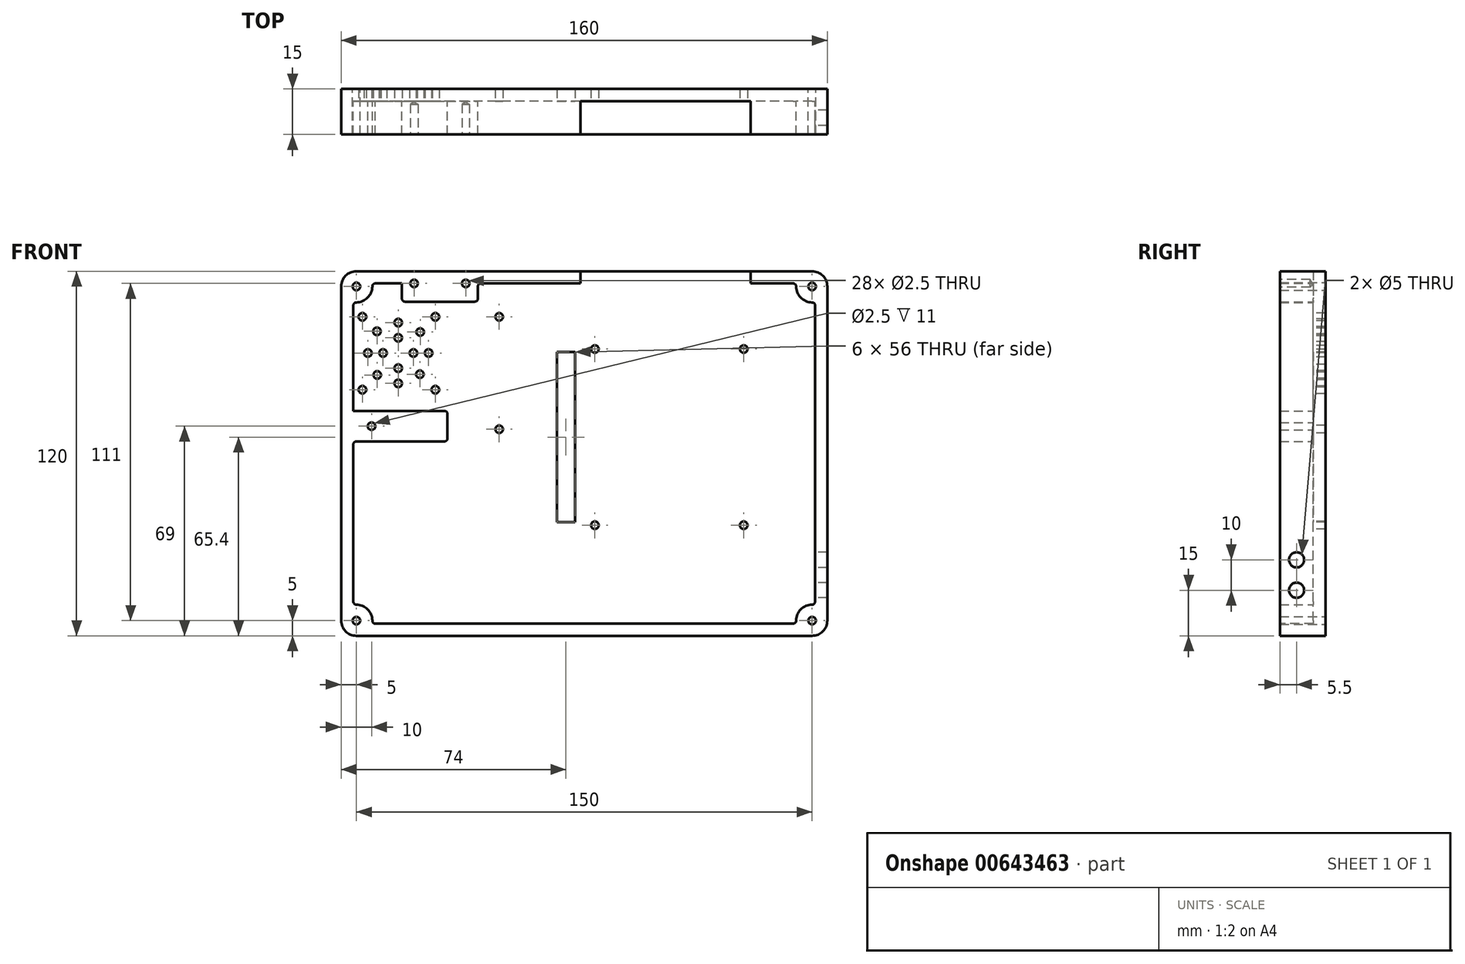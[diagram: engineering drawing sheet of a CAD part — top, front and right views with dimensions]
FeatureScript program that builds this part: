
annotation { "Feature Type Name" : "Feature", "Feature Type Description" : "" }
export const myFeature = defineFeature(function(context is Context, id is Id, definition is map)
    precondition{}
    {
        {
            var Q0;
            Q0=qCreatedBy(makeId("Front.planeOp"),FACE);
            var sketch = newSketch(context, id + "F0", { "sketchPlane" : qUnion([Q0])});
            skLineSegment(sketch, "E0.bottom", {"start": v(75, -60) * mm, "end": v(-75, -60) * mm});
            skLineSegment(sketch, "E0.top", {"start": v(75, 60) * mm, "end": v(-75, 60) * mm});
            skLineSegment(sketch, "E0.left", {"start": v(80, -55) * mm, "end": v(80, 55) * mm});
            skLineSegment(sketch, "E0.right", {"start": v(-80, -55) * mm, "end": v(-80, 55) * mm});
            skPoint(sketch, "E0.middle", {"position": v(0, 0) * mm});
            skPoint(sketch, "E1.visualSharp", {"position": v(-80, 60) * mm});
            skArc(sketch, "E1.filletArc", {"start": v(-75, 60) * mm, "mid": v(-78.54, 58.54) * mm, "end": v(-80, 55) * mm});
            skPoint(sketch, "E2.visualSharp", {"position": v(80, 60) * mm});
            skArc(sketch, "E2.filletArc", {"start": v(80, 55) * mm, "mid": v(78.54, 58.54) * mm, "end": v(75, 60) * mm});
            skPoint(sketch, "E3.visualSharp", {"position": v(80, -60) * mm});
            skArc(sketch, "E3.filletArc", {"start": v(75, -60) * mm, "mid": v(78.54, -58.54) * mm, "end": v(80, -55) * mm});
            skPoint(sketch, "E4.visualSharp", {"position": v(-80, -60) * mm});
            skArc(sketch, "E4.filletArc", {"start": v(-80, -55) * mm, "mid": v(-78.54, -58.54) * mm, "end": v(-75, -60) * mm});
            skSolve(sketch);
        }
        {
            var Q0;
            Q0=makeQuery(id+"F0.imprint","IMPRINT",FACE,{"disambiguationData":[TD([[makeQuery(id+"F0.imprint","IMPRINT",EDGE,{"derivedFrom":sQuery(id+"F0.wireOp",EDGE,"E0.bottom")}),-1.0]])]});
            extrude(context, id + "F1", {"entities" : qUnion([Q0]), "depth" : 15 * mm, "offsetDistance" : 25 * mm});
        }
        {
            var Q0;
            Q0=qCreatedBy(makeId("Front.planeOp"),FACE);
            var sketch = newSketch(context, id + "F2", { "sketchPlane" : qUnion([Q0])});
            skCircle(sketch, "E5", {"center": v(-75, 55) * mm, "radius": 1.25 * mm});
            skCircle(sketch, "E6", {"center": v(75, 55) * mm, "radius": 1.25 * mm});
            skCircle(sketch, "E7", {"center": v(75, -55) * mm, "radius": 1.25 * mm});
            skCircle(sketch, "E8", {"center": v(-75, -55) * mm, "radius": 1.25 * mm});
            skSolve(sketch);
        }
        {
            var Q0;
            Q0 = qSketchRegion(id + "F2", true);
            extrude(context, id + "F3", {"entities" : qUnion([Q0]), "operationType" : NewBodyOperationType.REMOVE, "depth" : 25 * mm, "offsetDistance" : 25 * mm});
        }
        {
            var Q0;
            Q0=makeQuery(id+"F1.opExtrude","CAP_FACE",FACE,{"disambiguationData":[OSD([sQuery(id+"F0.wireOp",EDGE,"E0.bottom"),sQuery(id+"F0.wireOp",EDGE,"E0.top"),sQuery(id+"F0.wireOp",EDGE,"E0.left"),sQuery(id+"F0.wireOp",EDGE,"E0.right"),sQuery(id+"F0.wireOp",EDGE,"E1.filletArc"),sQuery(id+"F0.wireOp",EDGE,"E2.filletArc"),sQuery(id+"F0.wireOp",EDGE,"E3.filletArc"),sQuery(id+"F0.wireOp",EDGE,"E4.filletArc")])],"isStart":false});
            shell(context, id + "F4", {"entities" : qUnion([Q0]), "thickness" : 4 * mm});
        }
        {
            var Q0;
            Q0=makeQuery(id+"F4.opShell","OFFSET_FACE",FACE,{"disambiguationData":[OSD([sQuery(id+"F0.wireOp",EDGE,"E0.bottom"),sQuery(id+"F0.wireOp",EDGE,"E0.top"),sQuery(id+"F0.wireOp",EDGE,"E0.left"),sQuery(id+"F0.wireOp",EDGE,"E0.right"),sQuery(id+"F0.wireOp",EDGE,"E1.filletArc"),sQuery(id+"F0.wireOp",EDGE,"E2.filletArc"),sQuery(id+"F0.wireOp",EDGE,"E3.filletArc"),sQuery(id+"F0.wireOp",EDGE,"E4.filletArc")])]});
            var sketch = newSketch(context, id + "F5", { "sketchPlane" : qUnion([Q0])});
            skPoint(sketch, "E9.start.orphan", {"position": v(0, -27.1) * mm});
            skCircle(sketch, "E10", {"center": v(3.5, 34.4) * mm, "radius": 1.25 * mm});
            skCircle(sketch, "E11", {"center": v(52.5, 34.4) * mm, "radius": 1.25 * mm});
            skCircle(sketch, "E12", {"center": v(52.5, -23.6) * mm, "radius": 1.25 * mm});
            skCircle(sketch, "E13", {"center": v(3.5, -23.6) * mm, "radius": 1.25 * mm});
            skSolve(sketch);
        }
        {
            var Q0;
            Q0=makeQuery(id+"F5.imprint","IMPRINT",FACE,{"disambiguationData":[TD([[makeQuery(id+"F5.imprint","IMPRINT",EDGE,{"derivedFrom":sQuery(id+"F5.wireOp",EDGE,"E10")}),1.0]])]});
            var Q1;
            Q1=makeQuery(id+"F5.imprint","IMPRINT",FACE,{"disambiguationData":[TD([[makeQuery(id+"F5.imprint","IMPRINT",EDGE,{"derivedFrom":sQuery(id+"F5.wireOp",EDGE,"E11")}),1.0]])]});
            var Q2;
            Q2=makeQuery(id+"F5.imprint","IMPRINT",FACE,{"disambiguationData":[TD([[makeQuery(id+"F5.imprint","IMPRINT",EDGE,{"derivedFrom":sQuery(id+"F5.wireOp",EDGE,"E12")}),1.0]])]});
            var Q3;
            Q3=makeQuery(id+"F5.imprint","IMPRINT",FACE,{"disambiguationData":[TD([[makeQuery(id+"F5.imprint","IMPRINT",EDGE,{"derivedFrom":sQuery(id+"F5.wireOp",EDGE,"E13")}),1.0]])]});
            extrude(context, id + "F6", {"entities" : qUnion([Q0, Q1, Q2, Q3]), "operationType" : NewBodyOperationType.REMOVE, "oppositeDirection" : true, "depth" : 25 * mm, "offsetDistance" : 25 * mm});
        }
        {
            var Q0;
            Q0=makeQuery(id+"F4.opShell","OFFSET_FACE",FACE,{"disambiguationData":[OSD([sQuery(id+"F0.wireOp",EDGE,"E0.bottom"),sQuery(id+"F0.wireOp",EDGE,"E0.top"),sQuery(id+"F0.wireOp",EDGE,"E0.left"),sQuery(id+"F0.wireOp",EDGE,"E0.right"),sQuery(id+"F0.wireOp",EDGE,"E1.filletArc"),sQuery(id+"F0.wireOp",EDGE,"E2.filletArc"),sQuery(id+"F0.wireOp",EDGE,"E3.filletArc"),sQuery(id+"F0.wireOp",EDGE,"E4.filletArc")])]});
            var sketch = newSketch(context, id + "F7", { "sketchPlane" : qUnion([Q0])});
            skLineSegment(sketch, "E14", {"start": v(-1.25, 60) * mm, "end": v(-1.25, 56) * mm});
            skLineSegment(sketch, "E15", {"start": v(54.75, 60) * mm, "end": v(54.75, 56) * mm});
            skLineSegment(sketch, "E16.0", {"start": v(54.75, 60) * mm, "end": v(-1.25, 60) * mm});
            skLineSegment(sketch, "E17.0", {"start": v(54.75, 56) * mm, "end": v(-1.25, 56) * mm});
            skPoint(sketch, "E18.orphan", {"position": v(69.85, 56) * mm});
            skPoint(sketch, "E19.orphan", {"position": v(-69.85, 56) * mm});
            skSolve(sketch);
        }
        {
            var Q0;
            Q0=makeQuery(id+"F7.imprint","IMPRINT",FACE,{"disambiguationData":[TD([[makeQuery(id+"F7.imprint","IMPRINT",EDGE,{"derivedFrom":sQuery(id+"F7.wireOp",EDGE,"E14")}),1.0]])]});
            extrude(context, id + "F8", {"entities" : qUnion([Q0]), "operationType" : NewBodyOperationType.REMOVE, "depth" : 25 * mm, "offsetDistance" : 25 * mm});
        }
        {
            var Q0;
            Q0=makeQuery(id+"F8.boolean.opBoolean","MERGE",FACE,{"derivedFrom":[makeQuery(id+"F4.opShell","OFFSET_FACE",FACE,{"disambiguationData":[OSD([sQuery(id+"F0.wireOp",EDGE,"E0.bottom"),sQuery(id+"F0.wireOp",EDGE,"E0.top"),sQuery(id+"F0.wireOp",EDGE,"E0.left"),sQuery(id+"F0.wireOp",EDGE,"E0.right"),sQuery(id+"F0.wireOp",EDGE,"E1.filletArc"),sQuery(id+"F0.wireOp",EDGE,"E2.filletArc"),sQuery(id+"F0.wireOp",EDGE,"E3.filletArc"),sQuery(id+"F0.wireOp",EDGE,"E4.filletArc")])]}),makeQuery(id+"F8.opExtrude","CAP_FACE",FACE,{"disambiguationData":[OSD([sQuery(id+"F7.wireOp",EDGE,"E14"),sQuery(id+"F7.wireOp",EDGE,"E15"),sQuery(id+"F7.wireOp",EDGE,"E16.0"),sQuery(id+"F7.wireOp",EDGE,"E17.0")])],"isStart":true})]});
            var sketch = newSketch(context, id + "F9", { "sketchPlane" : qUnion([Q0])});
            skLineSegment(sketch, "E20.0", {"start": v(-35, 56) * mm, "end": v(-60, 56) * mm});
            skLineSegment(sketch, "E21", {"start": v(-60, 56) * mm, "end": v(-60, 50) * mm});
            skLineSegment(sketch, "E22", {"start": v(-35, 56) * mm, "end": v(-35, 50) * mm});
            skLineSegment(sketch, "E23", {"start": v(-60, 50) * mm, "end": v(-35, 50) * mm});
            skPoint(sketch, "E24.orphan", {"position": v(-69.85, 56) * mm});
            skPoint(sketch, "E25.orphan", {"position": v(-1.25, 56) * mm});
            skSolve(sketch);
        }
        {
            var Q0;
            Q0 = qSketchRegion(id + "F9", true);
            extrude(context, id + "F10", {"entities" : qUnion([Q0]), "operationType" : NewBodyOperationType.ADD, "depth" : 11 * mm, "offsetDistance" : 25 * mm});
        }
        {
            var Q0;
            Q0=makeQuery(id+"F10.opExtrude","SWEPT_EDGE",EDGE,{"disambiguationData":[OSD([sQuery(id+"F0.wireOp",EDGE,"E0.top"),sQuery(id+"F9.wireOp",EDGE,"E20.0"),sQuery(id+"F9.wireOp",EDGE,"E21")])]});
            var Q1;
            Q1=makeQuery(id+"F10.opExtrude","SWEPT_EDGE",EDGE,{"disambiguationData":[OSD([sQuery(id+"F9.wireOp",EDGE,"E21"),sQuery(id+"F9.wireOp",EDGE,"E23")])]});
            var Q2;
            Q2=makeQuery(id+"F10.opExtrude","SWEPT_EDGE",EDGE,{"disambiguationData":[OSD([sQuery(id+"F9.wireOp",EDGE,"E22"),sQuery(id+"F9.wireOp",EDGE,"E23")])]});
            var Q3;
            Q3=makeQuery(id+"F10.opExtrude","SWEPT_EDGE",EDGE,{"disambiguationData":[OSD([sQuery(id+"F0.wireOp",EDGE,"E0.top"),sQuery(id+"F9.wireOp",EDGE,"E20.0"),sQuery(id+"F9.wireOp",EDGE,"E22")])]});
            fillet(context, id + "F11", {"entities" : qUnion([Q0, Q1, Q2, Q3]), "radius" : 1 * mm, "tangentPropagation" : true, "allowEdgeOverflow" : false});
        }
        {
            var Q0;
            Q0=makeQuery(id+"F10.boolean.opBoolean","MERGE",FACE,{"derivedFrom":[makeQuery(id+"F1.opExtrude","CAP_FACE",FACE,{"disambiguationData":[OSD([sQuery(id+"F0.wireOp",EDGE,"E0.bottom"),sQuery(id+"F0.wireOp",EDGE,"E0.top"),sQuery(id+"F0.wireOp",EDGE,"E0.left"),sQuery(id+"F0.wireOp",EDGE,"E0.right"),sQuery(id+"F0.wireOp",EDGE,"E1.filletArc"),sQuery(id+"F0.wireOp",EDGE,"E2.filletArc"),sQuery(id+"F0.wireOp",EDGE,"E3.filletArc"),sQuery(id+"F0.wireOp",EDGE,"E4.filletArc")])],"isStart":false}),makeQuery(id+"F10.opExtrude","CAP_FACE",FACE,{"disambiguationData":[OSD([sQuery(id+"F9.wireOp",EDGE,"E20.0"),sQuery(id+"F9.wireOp",EDGE,"E21"),sQuery(id+"F9.wireOp",EDGE,"E22"),sQuery(id+"F9.wireOp",EDGE,"E23")])],"isStart":false})]});
            var sketch = newSketch(context, id + "F12", { "sketchPlane" : qUnion([Q0])});
            skCircle(sketch, "E26", {"center": v(-56, 56) * mm, "radius": 1.25 * mm});
            skCircle(sketch, "E27", {"center": v(-39, 56) * mm, "radius": 1.25 * mm});
            skSolve(sketch);
        }
        {
            var Q0;
            Q0=sQuery(id+"F12.wireOp",VERTEX,"E26.center");
            var Q1;
            Q1=sQuery(id+"F12.wireOp",VERTEX,"E27.center");
            var Q2;
            Q2=makeQuery(id+"F1.opExtrude","SWEPT_BODY",BODY,{"disambiguationData":[OSD([sQuery(id+"F0.wireOp",EDGE,"E0.bottom"),sQuery(id+"F0.wireOp",EDGE,"E0.top"),sQuery(id+"F0.wireOp",EDGE,"E0.left"),sQuery(id+"F0.wireOp",EDGE,"E0.right"),sQuery(id+"F0.wireOp",EDGE,"E1.filletArc"),sQuery(id+"F0.wireOp",EDGE,"E2.filletArc"),sQuery(id+"F0.wireOp",EDGE,"E3.filletArc"),sQuery(id+"F0.wireOp",EDGE,"E4.filletArc")])]});
            hole(context, id + "F13", {"style" : HoleStyle.SIMPLE, "endStyle" : HoleEndStyle.BLIND, "holeDiameter" : 2.5 * mm, "majorDiameter" : 5 * mm, "holeDepth" : 10 * mm, "isTappedThrough" : true, "tappedDepth" : 12 * mm, "tapClearance" : 3, "startFromSketch" : true, "locations" : qUnion([Q0, Q1]), "scope" : qUnion([Q2])});
        }
        {
            var Q0;
            Q0=makeQuery(id+"F8.boolean.opBoolean","MERGE",FACE,{"derivedFrom":[makeQuery(id+"F4.opShell","OFFSET_FACE",FACE,{"disambiguationData":[OSD([sQuery(id+"F0.wireOp",EDGE,"E0.bottom"),sQuery(id+"F0.wireOp",EDGE,"E0.top"),sQuery(id+"F0.wireOp",EDGE,"E0.left"),sQuery(id+"F0.wireOp",EDGE,"E0.right"),sQuery(id+"F0.wireOp",EDGE,"E1.filletArc"),sQuery(id+"F0.wireOp",EDGE,"E2.filletArc"),sQuery(id+"F0.wireOp",EDGE,"E3.filletArc"),sQuery(id+"F0.wireOp",EDGE,"E4.filletArc")])]}),makeQuery(id+"F8.opExtrude","CAP_FACE",FACE,{"disambiguationData":[OSD([sQuery(id+"F7.wireOp",EDGE,"E14"),sQuery(id+"F7.wireOp",EDGE,"E15"),sQuery(id+"F7.wireOp",EDGE,"E16.0"),sQuery(id+"F7.wireOp",EDGE,"E17.0")])],"isStart":true})]});
            var sketch = newSketch(context, id + "F14", { "sketchPlane" : qUnion([Q0])});
            skCircle(sketch, "E28", {"center": v(-73, 45) * mm, "radius": 1.25 * mm});
            skCircle(sketch, "E29", {"center": v(-49, 45) * mm, "radius": 1.25 * mm});
            skCircle(sketch, "E30", {"center": v(-49, 21) * mm, "radius": 1.25 * mm});
            skCircle(sketch, "E31", {"center": v(-73, 21) * mm, "radius": 1.25 * mm});
            skSolve(sketch);
        }
        {
            var Q0;
            Q0=sQuery(id+"F14.wireOp",VERTEX,"E29.center");
            var Q1;
            Q1=sQuery(id+"F14.wireOp",VERTEX,"E28.center");
            var Q2;
            Q2=sQuery(id+"F14.wireOp",VERTEX,"E31.center");
            var Q3;
            Q3=sQuery(id+"F14.wireOp",VERTEX,"E30.center");
            var Q4;
            Q4=makeQuery(id+"F1.opExtrude","SWEPT_BODY",BODY,{"disambiguationData":[OSD([sQuery(id+"F0.wireOp",EDGE,"E0.bottom"),sQuery(id+"F0.wireOp",EDGE,"E0.top"),sQuery(id+"F0.wireOp",EDGE,"E0.left"),sQuery(id+"F0.wireOp",EDGE,"E0.right"),sQuery(id+"F0.wireOp",EDGE,"E1.filletArc"),sQuery(id+"F0.wireOp",EDGE,"E2.filletArc"),sQuery(id+"F0.wireOp",EDGE,"E3.filletArc"),sQuery(id+"F0.wireOp",EDGE,"E4.filletArc")])]});
            hole(context, id + "F15", {"style" : HoleStyle.SIMPLE, "endStyle" : HoleEndStyle.BLIND, "holeDiameter" : 2.5 * mm, "majorDiameter" : 5 * mm, "holeDepth" : 10 * mm, "isTappedThrough" : true, "tappedDepth" : 12 * mm, "tapClearance" : 3, "startFromSketch" : true, "locations" : qUnion([Q0, Q1, Q2, Q3]), "scope" : qUnion([Q4])});
        }
        {
            var Q0;
            Q0=makeQuery(id+"F8.boolean.opBoolean","MERGE",FACE,{"derivedFrom":[makeQuery(id+"F4.opShell","OFFSET_FACE",FACE,{"disambiguationData":[OSD([sQuery(id+"F0.wireOp",EDGE,"E0.bottom"),sQuery(id+"F0.wireOp",EDGE,"E0.top"),sQuery(id+"F0.wireOp",EDGE,"E0.left"),sQuery(id+"F0.wireOp",EDGE,"E0.right"),sQuery(id+"F0.wireOp",EDGE,"E1.filletArc"),sQuery(id+"F0.wireOp",EDGE,"E2.filletArc"),sQuery(id+"F0.wireOp",EDGE,"E3.filletArc"),sQuery(id+"F0.wireOp",EDGE,"E4.filletArc")])]}),makeQuery(id+"F8.opExtrude","CAP_FACE",FACE,{"disambiguationData":[OSD([sQuery(id+"F7.wireOp",EDGE,"E14"),sQuery(id+"F7.wireOp",EDGE,"E15"),sQuery(id+"F7.wireOp",EDGE,"E16.0"),sQuery(id+"F7.wireOp",EDGE,"E17.0")])],"isStart":true})]});
            var sketch = newSketch(context, id + "F16", { "sketchPlane" : qUnion([Q0])});
            skLineSegment(sketch, "E32", {"start": v(-76, 4) * mm, "end": v(-46, 4) * mm});
            skLineSegment(sketch, "E33", {"start": v(-76, 14) * mm, "end": v(-46, 14) * mm});
            skLineSegment(sketch, "E34.0", {"start": v(-76, 4) * mm, "end": v(-76, 14) * mm});
            skLineSegment(sketch, "E35", {"start": v(-45, 13) * mm, "end": v(-45, 5) * mm});
            skCircle(sketch, "E36", {"center": v(-70, 9) * mm, "radius": 1.25 * mm});
            skPoint(sketch, "E37.orphan", {"position": v(-76, 49.85) * mm});
            skPoint(sketch, "E38.orphan", {"position": v(-76, -49.85) * mm});
            skPoint(sketch, "E39.visualSharp", {"position": v(-45, 14) * mm});
            skArc(sketch, "E39.filletArc", {"start": v(-45, 13) * mm, "mid": v(-45.3, 13.7) * mm, "end": v(-46, 14) * mm});
            skPoint(sketch, "E40.visualSharp", {"position": v(-45, 4) * mm});
            skArc(sketch, "E40.filletArc", {"start": v(-46, 4) * mm, "mid": v(-45.3, 4.3) * mm, "end": v(-45, 5) * mm});
            skSolve(sketch);
        }
        {
            var Q0;
            Q0 = qSketchRegion(id + "F16", true);
            extrude(context, id + "F17", {"entities" : qUnion([Q0]), "operationType" : NewBodyOperationType.ADD, "depth" : 11 * mm, "offsetDistance" : 25 * mm});
        }
        {
            var Q0;
            Q0=makeQuery(id+"F4.opShell","TWEAK_EDGE",EDGE,{"derivedFrom":[makeQuery(id+"F1.opExtrude","SWEPT_FACE",FACE,{"disambiguationData":[OSD([sQuery(id+"F0.wireOp",EDGE,"E0.top")])]}),makeQuery(id+"F3.boolean.opBoolean","COPY",FACE,{"derivedFrom":makeQuery(id+"F3.opExtrude","SWEPT_FACE",FACE,{"disambiguationData":[OSD([sQuery(id+"F2.wireOp",EDGE,"E5")])]})})]});
            var Q1;
            Q1=makeQuery(id+"F4.opShell","TWEAK_EDGE",EDGE,{"derivedFrom":[makeQuery(id+"F1.opExtrude","SWEPT_FACE",FACE,{"disambiguationData":[OSD([sQuery(id+"F0.wireOp",EDGE,"E0.right")])]}),makeQuery(id+"F3.boolean.opBoolean","COPY",FACE,{"derivedFrom":makeQuery(id+"F3.opExtrude","SWEPT_FACE",FACE,{"disambiguationData":[OSD([sQuery(id+"F2.wireOp",EDGE,"E5")])]})})]});
            var Q2;
            Q2=makeQuery(id+"F4.opShell","TWEAK_EDGE",EDGE,{"derivedFrom":[makeQuery(id+"F1.opExtrude","SWEPT_FACE",FACE,{"disambiguationData":[OSD([sQuery(id+"F0.wireOp",EDGE,"E0.right")])]}),makeQuery(id+"F3.boolean.opBoolean","COPY",FACE,{"derivedFrom":makeQuery(id+"F3.opExtrude","SWEPT_FACE",FACE,{"disambiguationData":[OSD([sQuery(id+"F2.wireOp",EDGE,"E8")])]})})]});
            var Q3;
            Q3=makeQuery(id+"F4.opShell","TWEAK_EDGE",EDGE,{"derivedFrom":[makeQuery(id+"F1.opExtrude","SWEPT_FACE",FACE,{"disambiguationData":[OSD([sQuery(id+"F0.wireOp",EDGE,"E0.bottom")])]}),makeQuery(id+"F3.boolean.opBoolean","COPY",FACE,{"derivedFrom":makeQuery(id+"F3.opExtrude","SWEPT_FACE",FACE,{"disambiguationData":[OSD([sQuery(id+"F2.wireOp",EDGE,"E8")])]})})]});
            var Q4;
            Q4=makeQuery(id+"F4.opShell","TWEAK_EDGE",EDGE,{"derivedFrom":[makeQuery(id+"F1.opExtrude","SWEPT_FACE",FACE,{"disambiguationData":[OSD([sQuery(id+"F0.wireOp",EDGE,"E0.bottom")])]}),makeQuery(id+"F3.boolean.opBoolean","COPY",FACE,{"derivedFrom":makeQuery(id+"F3.opExtrude","SWEPT_FACE",FACE,{"disambiguationData":[OSD([sQuery(id+"F2.wireOp",EDGE,"E7")])]})})]});
            var Q5;
            Q5=makeQuery(id+"F4.opShell","TWEAK_EDGE",EDGE,{"derivedFrom":[makeQuery(id+"F1.opExtrude","SWEPT_FACE",FACE,{"disambiguationData":[OSD([sQuery(id+"F0.wireOp",EDGE,"E0.left")])]}),makeQuery(id+"F3.boolean.opBoolean","COPY",FACE,{"derivedFrom":makeQuery(id+"F3.opExtrude","SWEPT_FACE",FACE,{"disambiguationData":[OSD([sQuery(id+"F2.wireOp",EDGE,"E7")])]})})]});
            var Q6;
            Q6=makeQuery(id+"F4.opShell","TWEAK_EDGE",EDGE,{"derivedFrom":[makeQuery(id+"F1.opExtrude","SWEPT_FACE",FACE,{"disambiguationData":[OSD([sQuery(id+"F0.wireOp",EDGE,"E0.left")])]}),makeQuery(id+"F3.boolean.opBoolean","COPY",FACE,{"derivedFrom":makeQuery(id+"F3.opExtrude","SWEPT_FACE",FACE,{"disambiguationData":[OSD([sQuery(id+"F2.wireOp",EDGE,"E6")])]})})]});
            var Q7;
            Q7=makeQuery(id+"F4.opShell","TWEAK_EDGE",EDGE,{"derivedFrom":[makeQuery(id+"F1.opExtrude","SWEPT_FACE",FACE,{"disambiguationData":[OSD([sQuery(id+"F0.wireOp",EDGE,"E0.top")])]}),makeQuery(id+"F3.boolean.opBoolean","COPY",FACE,{"derivedFrom":makeQuery(id+"F3.opExtrude","SWEPT_FACE",FACE,{"disambiguationData":[OSD([sQuery(id+"F2.wireOp",EDGE,"E6")])]})})]});
            var Q8;
            Q8=makeQuery(id+"F17.opExtrude","SWEPT_EDGE",EDGE,{"disambiguationData":[OSD([sQuery(id+"F0.wireOp",EDGE,"E0.right"),sQuery(id+"F16.wireOp",EDGE,"E33"),sQuery(id+"F16.wireOp",EDGE,"E34.0")])]});
            var Q9;
            Q9=makeQuery(id+"F17.opExtrude","SWEPT_EDGE",EDGE,{"disambiguationData":[OSD([sQuery(id+"F16.wireOp",EDGE,"E33"),sQuery(id+"F16.wireOp",EDGE,"E35")])]});
            var Q10;
            Q10=makeQuery(id+"F17.opExtrude","SWEPT_EDGE",EDGE,{"disambiguationData":[OSD([sQuery(id+"F16.wireOp",EDGE,"E32"),sQuery(id+"F16.wireOp",EDGE,"E35")])]});
            var Q11;
            Q11=makeQuery(id+"F17.opExtrude","SWEPT_EDGE",EDGE,{"disambiguationData":[OSD([sQuery(id+"F0.wireOp",EDGE,"E0.right"),sQuery(id+"F16.wireOp",EDGE,"E32"),sQuery(id+"F16.wireOp",EDGE,"E34.0")])]});
            fillet(context, id + "F18", {"entities" : qUnion([Q0, Q1, Q2, Q3, Q4, Q5, Q6, Q7, Q8, Q9, Q10, Q11]), "radius" : 1 * mm, "tangentPropagation" : true, "allowEdgeOverflow" : false});
        }
        {
            var Q0;
            Q0=makeQuery(id+"F8.boolean.opBoolean","MERGE",FACE,{"derivedFrom":[makeQuery(id+"F4.opShell","OFFSET_FACE",FACE,{"disambiguationData":[OSD([sQuery(id+"F0.wireOp",EDGE,"E0.bottom"),sQuery(id+"F0.wireOp",EDGE,"E0.top"),sQuery(id+"F0.wireOp",EDGE,"E0.left"),sQuery(id+"F0.wireOp",EDGE,"E0.right"),sQuery(id+"F0.wireOp",EDGE,"E1.filletArc"),sQuery(id+"F0.wireOp",EDGE,"E2.filletArc"),sQuery(id+"F0.wireOp",EDGE,"E3.filletArc"),sQuery(id+"F0.wireOp",EDGE,"E4.filletArc")])]}),makeQuery(id+"F8.opExtrude","CAP_FACE",FACE,{"disambiguationData":[OSD([sQuery(id+"F7.wireOp",EDGE,"E14"),sQuery(id+"F7.wireOp",EDGE,"E15"),sQuery(id+"F7.wireOp",EDGE,"E16.0"),sQuery(id+"F7.wireOp",EDGE,"E17.0")])],"isStart":true})]});
            var sketch = newSketch(context, id + "F19", { "sketchPlane" : qUnion([Q0])});
            skCircle(sketch, "E41", {"center": v(-61.22, 43.1) * mm, "radius": 1.5 * mm});
            skCircle(sketch, "E42.MirrorC", {"center": v(-61.22, 23.1) * mm, "radius": 1.5 * mm});
            skCircle(sketch, "E43", {"center": v(-51.22, 33.1) * mm, "radius": 1.5 * mm});
            skCircle(sketch, "E44.MirrorC", {"center": v(-71.22, 33.1) * mm, "radius": 1.5 * mm});
            skCircle(sketch, "E45", {"center": v(-61.22, 38.1) * mm, "radius": 1.5 * mm});
            skCircle(sketch, "E46", {"center": v(-56.22, 33.1) * mm, "radius": 1.5 * mm});
            skCircle(sketch, "E47.MirrorC", {"center": v(-66.22, 33.1) * mm, "radius": 1.5 * mm});
            skCircle(sketch, "E48.MirrorC", {"center": v(-61.22, 28.1) * mm, "radius": 1.5 * mm});
            skPoint(sketch, "E49.orphan", {"position": v(-73, 45) * mm});
            skPoint(sketch, "E50.orphan", {"position": v(-49, 45) * mm});
            skPoint(sketch, "E51.orphan", {"position": v(-49, 21) * mm});
            skPoint(sketch, "E52.orphan", {"position": v(-73, 21) * mm});
            skCircle(sketch, "E53", {"center": v(-68.23, 40.23) * mm, "radius": 1.5 * mm});
            skCircle(sketch, "E54", {"center": v(-54, 40) * mm, "radius": 1.5 * mm});
            skCircle(sketch, "E55", {"center": v(-54.09, 26.09) * mm, "radius": 1.5 * mm});
            skCircle(sketch, "E56", {"center": v(-68.13, 25.87) * mm, "radius": 1.5 * mm});
            skSolve(sketch);
        }
        {
            var Q0;
            Q0=sQuery(id+"F19.wireOp",VERTEX,"E41.center");
            var Q1;
            Q1=sQuery(id+"F19.wireOp",VERTEX,"E45.center");
            var Q2;
            Q2=sQuery(id+"F19.wireOp",VERTEX,"E53.center");
            var Q3;
            Q3=sQuery(id+"F19.wireOp",VERTEX,"E44.MirrorC.center");
            var Q4;
            Q4=sQuery(id+"F19.wireOp",VERTEX,"E47.MirrorC.center");
            var Q5;
            Q5=sQuery(id+"F19.wireOp",VERTEX,"E56.center");
            var Q6;
            Q6=sQuery(id+"F19.wireOp",VERTEX,"E48.MirrorC.center");
            var Q7;
            Q7=sQuery(id+"F19.wireOp",VERTEX,"E42.MirrorC.center");
            var Q8;
            Q8=sQuery(id+"F19.wireOp",VERTEX,"E54.center");
            var Q9;
            Q9=sQuery(id+"F19.wireOp",VERTEX,"E46.center");
            var Q10;
            Q10=sQuery(id+"F19.wireOp",VERTEX,"E55.center");
            var Q11;
            Q11=sQuery(id+"F19.wireOp",VERTEX,"E43.center");
            var Q12;
            Q12=makeQuery(id+"F1.opExtrude","SWEPT_BODY",BODY,{"disambiguationData":[OSD([sQuery(id+"F0.wireOp",EDGE,"E0.bottom"),sQuery(id+"F0.wireOp",EDGE,"E0.top"),sQuery(id+"F0.wireOp",EDGE,"E0.left"),sQuery(id+"F0.wireOp",EDGE,"E0.right"),sQuery(id+"F0.wireOp",EDGE,"E1.filletArc"),sQuery(id+"F0.wireOp",EDGE,"E2.filletArc"),sQuery(id+"F0.wireOp",EDGE,"E3.filletArc"),sQuery(id+"F0.wireOp",EDGE,"E4.filletArc")])]});
            hole(context, id + "F20", {"style" : HoleStyle.SIMPLE, "endStyle" : HoleEndStyle.BLIND, "holeDiameter" : 2.5 * mm, "majorDiameter" : 5 * mm, "holeDepth" : 10 * mm, "isTappedThrough" : true, "tappedDepth" : 12 * mm, "tapClearance" : 3, "startFromSketch" : true, "locations" : qUnion([Q0, Q1, Q2, Q3, Q4, Q5, Q6, Q7, Q8, Q9, Q10, Q11]), "scope" : qUnion([Q12])});
        }
        {
            var Q0;
            Q0=makeQuery(id+"F8.boolean.opBoolean","MERGE",FACE,{"derivedFrom":[makeQuery(id+"F4.opShell","OFFSET_FACE",FACE,{"disambiguationData":[OSD([sQuery(id+"F0.wireOp",EDGE,"E0.bottom"),sQuery(id+"F0.wireOp",EDGE,"E0.top"),sQuery(id+"F0.wireOp",EDGE,"E0.left"),sQuery(id+"F0.wireOp",EDGE,"E0.right"),sQuery(id+"F0.wireOp",EDGE,"E1.filletArc"),sQuery(id+"F0.wireOp",EDGE,"E2.filletArc"),sQuery(id+"F0.wireOp",EDGE,"E3.filletArc"),sQuery(id+"F0.wireOp",EDGE,"E4.filletArc")])]}),makeQuery(id+"F8.opExtrude","CAP_FACE",FACE,{"disambiguationData":[OSD([sQuery(id+"F7.wireOp",EDGE,"E14"),sQuery(id+"F7.wireOp",EDGE,"E15"),sQuery(id+"F7.wireOp",EDGE,"E16.0"),sQuery(id+"F7.wireOp",EDGE,"E17.0")])],"isStart":true})]});
            var sketch = newSketch(context, id + "F21", { "sketchPlane" : qUnion([Q0])});
            skLineSegment(sketch, "E57", {"start": v(-3, 33.4) * mm, "end": v(-3, -22.6) * mm});
            skLineSegment(sketch, "E58", {"start": v(-9, 33.4) * mm, "end": v(-9, -22.6) * mm});
            skLineSegment(sketch, "E59", {"start": v(-9, 33.4) * mm, "end": v(-3, 33.4) * mm});
            skLineSegment(sketch, "E60.MirrorCS", {"start": v(-9, -22.6) * mm, "end": v(-3, -22.6) * mm});
            skSolve(sketch);
        }
        {
            var Q0;
            Q0=makeQuery(id+"F21.imprint","IMPRINT",FACE,{"disambiguationData":[TD([[makeQuery(id+"F21.imprint","IMPRINT",EDGE,{"derivedFrom":sQuery(id+"F21.wireOp",EDGE,"E57")}),-1.0]])]});
            extrude(context, id + "F22", {"entities" : qUnion([Q0]), "operationType" : NewBodyOperationType.REMOVE, "oppositeDirection" : true, "depth" : 25 * mm, "offsetDistance" : 25 * mm});
        }
        {
            var Q0;
            Q0=qCreatedBy(makeId("Right.planeOp"),FACE);
            var sketch = newSketch(context, id + "F23", { "sketchPlane" : qUnion([Q0])});
            skCircle(sketch, "E61", {"center": v(-9.5, -35) * mm, "radius": 2.5 * mm});
            skCircle(sketch, "E62", {"center": v(-9.5, -45) * mm, "radius": 2.5 * mm});
            skSolve(sketch);
        }
        {
            var Q0;
            Q0=sQuery(id+"F23.wireOp",VERTEX,"E61.center");
            var Q1;
            Q1=sQuery(id+"F23.wireOp",VERTEX,"E62.center");
            var Q2;
            Q2=makeQuery(id+"F1.opExtrude","SWEPT_BODY",BODY,{"disambiguationData":[OSD([sQuery(id+"F0.wireOp",EDGE,"E0.bottom"),sQuery(id+"F0.wireOp",EDGE,"E0.top"),sQuery(id+"F0.wireOp",EDGE,"E0.left"),sQuery(id+"F0.wireOp",EDGE,"E0.right"),sQuery(id+"F0.wireOp",EDGE,"E1.filletArc"),sQuery(id+"F0.wireOp",EDGE,"E2.filletArc"),sQuery(id+"F0.wireOp",EDGE,"E3.filletArc"),sQuery(id+"F0.wireOp",EDGE,"E4.filletArc")])]});
            hole(context, id + "F24", {"style" : HoleStyle.SIMPLE, "endStyle" : HoleEndStyle.BLIND, "oppositeDirection" : true, "holeDiameter" : 5 * mm, "majorDiameter" : 5 * mm, "holeDepth" : 100 * mm, "isTappedThrough" : true, "tappedDepth" : 12 * mm, "tapClearance" : 3, "startFromSketch" : true, "locations" : qUnion([Q0, Q1]), "scope" : qUnion([Q2])});
        }
        {
            var Q0;
            {var subQ3=sQuery(id+"F0.wireOp",EDGE,"E0.top");var subQ5=sQuery(id+"F0.wireOp",EDGE,"E0.left");var subQ6=sQuery(id+"F0.wireOp",EDGE,"E0.bottom");var subQ7=sQuery(id+"F7.wireOp",EDGE,"E15");var subQ8=sQuery(id+"F0.wireOp",EDGE,"E0.right");var subQ9=sQuery(id+"F7.wireOp",EDGE,"E14");Q0=makeQuery(id+"F17.boolean.opBoolean","SPLIT",FACE,{"disambiguationData":[TD([makeQuery(id+"F1.opExtrude","SWEPT_FACE",FACE,{"disambiguationData":[OSD([subQ3])]})])],"derivedFrom":makeQuery(id+"F8.boolean.opBoolean","MERGE",FACE,{"derivedFrom":[makeQuery(id+"F4.opShell","OFFSET_FACE",FACE,{"disambiguationData":[OSD([subQ6,subQ3,subQ5,subQ8,sQuery(id+"F0.wireOp",EDGE,"E1.filletArc"),sQuery(id+"F0.wireOp",EDGE,"E2.filletArc"),sQuery(id+"F0.wireOp",EDGE,"E3.filletArc"),sQuery(id+"F0.wireOp",EDGE,"E4.filletArc")])]}),makeQuery(id+"F8.opExtrude","CAP_FACE",FACE,{"disambiguationData":[OSD([subQ9,subQ7,sQuery(id+"F7.wireOp",EDGE,"E16.0"),sQuery(id+"F7.wireOp",EDGE,"E17.0")])],"isStart":true})]})});}
            var sketch = newSketch(context, id + "F25", { "sketchPlane" : qUnion([Q0])});
            skCircle(sketch, "E63", {"center": v(-28, 45) * mm, "radius": 1.25 * mm});
            skCircle(sketch, "E64", {"center": v(-28, 8) * mm, "radius": 1.25 * mm});
            skSolve(sketch);
        }
        {
            var Q0;
            Q0=makeQuery(id+"F25.imprint","IMPRINT",FACE,{"disambiguationData":[TD([[makeQuery(id+"F25.imprint","IMPRINT",EDGE,{"derivedFrom":sQuery(id+"F25.wireOp",EDGE,"E63")}),1.0]])]});
            var Q1;
            Q1=makeQuery(id+"F25.imprint","IMPRINT",FACE,{"disambiguationData":[TD([[makeQuery(id+"F25.imprint","IMPRINT",EDGE,{"derivedFrom":sQuery(id+"F25.wireOp",EDGE,"E64")}),1.0]])]});
            extrude(context, id + "F26", {"entities" : qUnion([Q0, Q1]), "operationType" : NewBodyOperationType.REMOVE, "oppositeDirection" : true, "depth" : 5 * mm, "offsetDistance" : 25 * mm});
        }
    });
